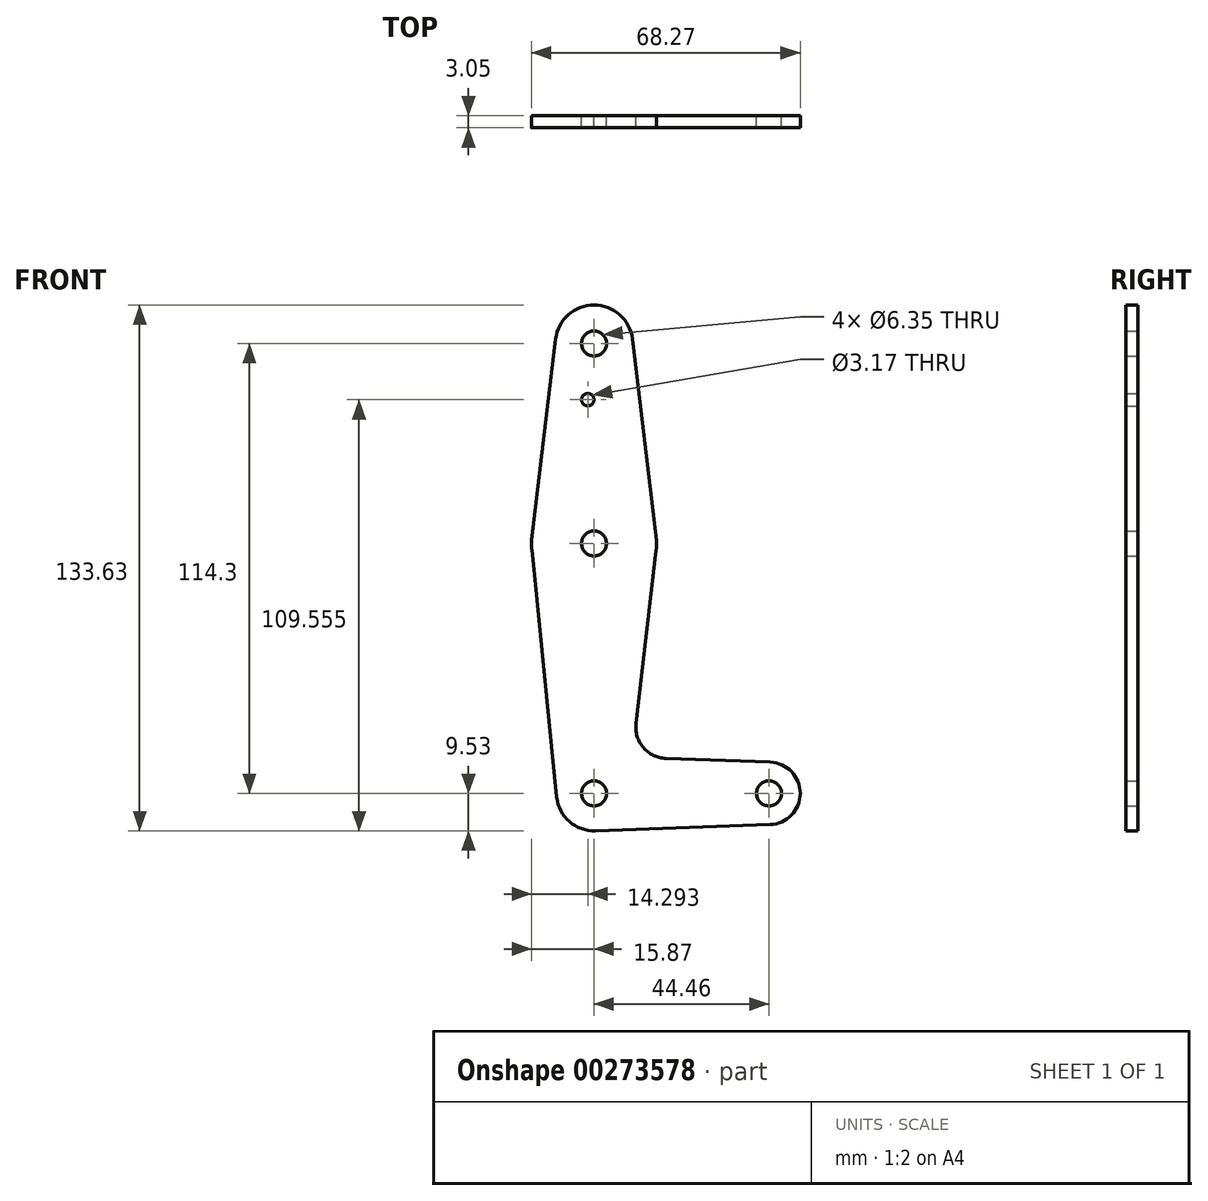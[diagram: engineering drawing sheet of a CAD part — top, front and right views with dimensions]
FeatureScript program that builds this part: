
annotation { "Feature Type Name" : "Feature", "Feature Type Description" : "" }
export const myFeature = defineFeature(function(context is Context, id is Id, definition is map)
    precondition{}
    {
        {
            var Q0;
            Q0=qCreatedBy(makeId("Front.planeOp"),FACE);
            var sketch = newSketch(context, id + "F0", { "sketchPlane" : qUnion([Q0])});
            skCircle(sketch, "E0", {"center": v(0, 114.3) * mm, "radius": 9.8 * mm});
            skCircle(sketch, "E1", {"center": v(0, 0) * mm, "radius": 9.53 * mm});
            skCircle(sketch, "E2", {"center": v(0, 63.5) * mm, "radius": 15.88 * mm});
            skLineSegment(sketch, "E3", {"start": v(-9.73, 115.47) * mm, "end": v(-15.77, 65.4) * mm});
            skLineSegment(sketch, "E4", {"start": v(9.73, 115.47) * mm, "end": v(15.75, 65.4) * mm});
            skCircle(sketch, "E5", {"center": v(0, 0) * mm, "radius": 3.18 * mm});
            skCircle(sketch, "E6", {"center": v(0, 63.5) * mm, "radius": 3.18 * mm});
            skCircle(sketch, "E7", {"center": v(0, 114.3) * mm, "radius": 3.18 * mm});
            skCircle(sketch, "E8", {"center": v(44.45, 0) * mm, "radius": 3.18 * mm});
            skCircle(sketch, "E9", {"center": v(-1.59, 100.03) * mm, "radius": 1.59 * mm});
            skLineSegment(sketch, "E10", {"start": v(0, 0) * mm, "end": v(44.45, 0) * mm, "construction": true});
            skCircle(sketch, "E11", {"center": v(44.45, 0) * mm, "radius": 7.94 * mm});
            skLineSegment(sketch, "E12", {"start": v(18.27, 8.88) * mm, "end": v(44.73, 7.93) * mm});
            skLineSegment(sketch, "E13", {"start": v(15.76, 61.67) * mm, "end": v(10.66, 17.74) * mm});
            skArc(sketch, "E14.filletArc", {"start": v(10.66, 17.74) * mm, "mid": v(12.53, 11.64) * mm, "end": v(18.27, 8.88) * mm});
            skLineSegment(sketch, "E15", {"start": v(0.34, -9.52) * mm, "end": v(44.73, -7.93) * mm});
            skLineSegment(sketch, "E16", {"start": v(0, 114.3) * mm, "end": v(0, 0) * mm, "construction": true});
            skLineSegment(sketch, "E17", {"start": v(0, 47.63) * mm, "end": v(0, 9.52) * mm});
            skLineSegment(sketch, "E18", {"start": v(-15.8, 61.91) * mm, "end": v(-9.48, -0.95) * mm});
            skSolve(sketch);
        }
        {
            var Q0;
            Q0 = qSketchRegion(id + "F0", true);
            extrude(context, id + "F1", {"entities" : qUnion([Q0]), "depth" : 3.05 * mm});
        }
    });
